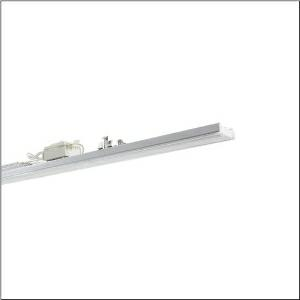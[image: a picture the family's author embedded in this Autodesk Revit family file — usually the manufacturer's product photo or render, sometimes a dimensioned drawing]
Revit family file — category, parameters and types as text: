
# Revit family: licross_r__11_recessed_mo_51te12dn4axg3s_81e1
name_source: partatom
category: Lighting Fixtures
units: mm (PartAtom-declared; Revit-internal decimal feet)

## family parameters
Cut with Voids When Loaded = No
Host = Face
Light Source = No
Part Type = Normal
Room Calculation Point = No
Round Connector Dimension = Use Diameter
Shared = No

## types (1)
- --- (1 x LED, 1010 lm, 6.7 W, 4000K)
    Apparent Load = 7 VA
    CIE Flux Codes = 67 92 99 100 100
    Color Rendering = 80
    Color Temperature = 4000K
    Default Elevation = 1800 mm
    Description = Licross® 11 Recessed MO, luminaire insert, of sheet steel, galvanised, coil coated, white, length: 1.500mm, width: 66mm, height: 67mm, LED rated luminous flux: 10.240lm, light colour: 840, control gear: DALI 2 (for two DALI lines), with plug, 6-pole, with phase selection, for trunking rail, 14-core, mains connection: 220..240V, AC, 50/60Hz, rated input power: 61W, for trunking rail, 14-core, halogen-free wiring, for emergency light function, converter,control gear: single battery element, battery: LiFePO4, 9Ah, primary optical cover: cover, of PMMA, light emission: direct distribution, primary light characteristic: symmetric, protection rating (complete): IP54, insulation class (complete): insulation class I (protective earthing), certification: CE, UKCA, protection symbol: D if used in an environment with non-conductive dust loads with corresponding accessories, impact resistance: IK06, permissible ambient temperature for indoor applications: +5..+35°C, standard: EN 60598-2-22, LABS conformity tested according to VDMA 24364:2018-05, reducing of maximum allowable ambient temperature of 5°C with ceiling mounting, corresponds to IFS (International Featured Standards) requirements for safety and quality in the food industry, packaging unit: 1 piece
    Height = 58 mm
    Lamp = 1 x LED
    Lamp Light Flux = 1010 lm
    Lamp Power = 6.7 W
    Lamp count = 1
    Length = 1500 mm
    Luminous efficacy = 151 lm/W
    Manufacturer = Siteco
    ModVariant = No
    Model = 51TE12DN4AXG3S
    Mounting Place = Ceiling
    Mounting Type = Pendant
    Number of Poles = 1
    OnlyDefault = Yes
    Power Factor = 1
    Product Name = Licross® 11 Recessed MO
    Product group = luminaire insert
    ProductGroupID = 902
    Protection Class = Protection class I
    Protection Degree = IP 54
    RLX_Detail_Level = 1
    RLX_Emergency_Light_Flux = 0 lm
    RLX_Emergency_Type = 0
    RLX_Emergency_Type_DB = No
    RlxData = <blob elided: 24777 chars, md5=8da48e42>
    Socket = socket
    Standby Power = 0 W
    System Light Flux = 1010 lm
    System Power = 7 W
    Type Comments = : emergency light operation: 3 h
    Type Image = l_1296930.jpg
    URL = http://relux.com
    VarID = @adj_090264
    Voltage = 0 V
    Weight = 0.00 kg
    Width = 66 mm

## geometry (parser evidence)
native form markers: Blend x4, Sweep x11
no freeform markers — native parametric forms only
